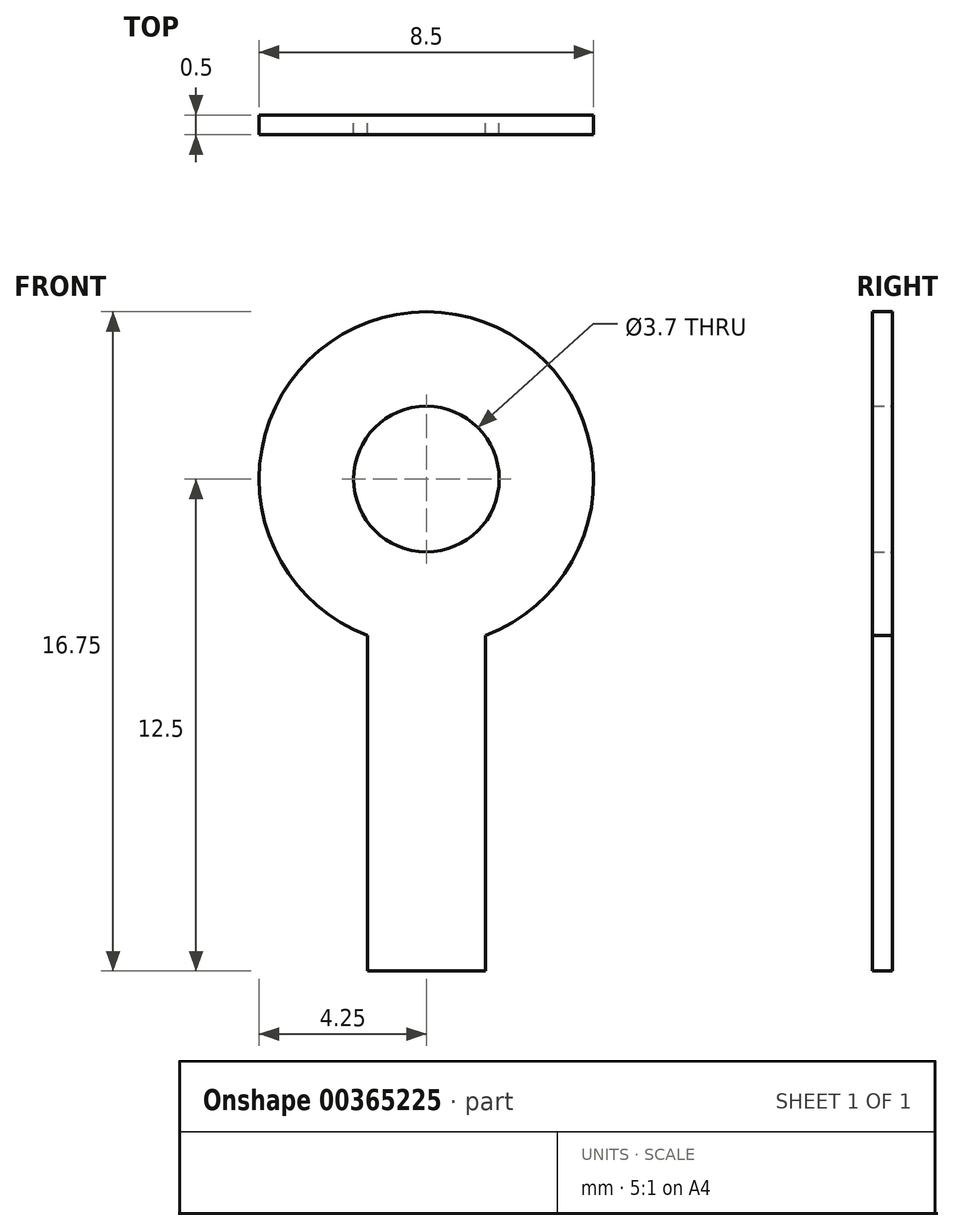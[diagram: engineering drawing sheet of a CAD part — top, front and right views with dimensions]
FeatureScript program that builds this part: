
annotation { "Feature Type Name" : "Feature", "Feature Type Description" : "" }
export const myFeature = defineFeature(function(context is Context, id is Id, definition is map)
    precondition{}
    {
        {
            var Q0;
            Q0=qCreatedBy(makeId("Front.planeOp"),FACE);
            var sketch = newSketch(context, id + "F0", { "sketchPlane" : qUnion([Q0])});
            skCircle(sketch, "E0", {"center": v(0, 0) * mm, "radius": 1.85 * mm});
            skArc(sketch, "E1", {"start": v(1.5, -3.98) * mm, "mid": v(0, 4.25) * mm, "end": v(-1.5, -3.98) * mm});
            skLineSegment(sketch, "E2.bottom", {"start": v(1.5, -12.5) * mm, "end": v(-1.5, -12.5) * mm});
            skLineSegment(sketch, "E2.left", {"start": v(1.5, -12.5) * mm, "end": v(1.5, -3.98) * mm});
            skLineSegment(sketch, "E2.right", {"start": v(-1.5, -12.5) * mm, "end": v(-1.5, -3.98) * mm});
            skPoint(sketch, "E2.top.end.orphan", {"position": v(-1.5, 12.5) * mm});
            skPoint(sketch, "E2.top.start.orphan", {"position": v(1.5, 12.5) * mm});
            skSolve(sketch);
        }
        {
            var Q0;
            Q0 = qSketchRegion(id + "F0", true);
            extrude(context, id + "F1", {"entities" : qUnion([Q0]), "depth" : .5 * mm});
        }
    });
